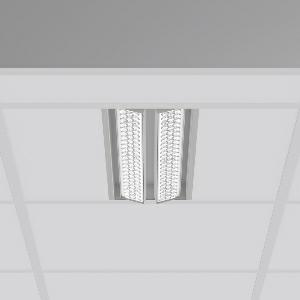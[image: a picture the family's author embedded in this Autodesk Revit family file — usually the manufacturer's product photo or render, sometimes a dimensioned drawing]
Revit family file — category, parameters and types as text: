
# Revit family: tx-move_901732_004_76_082e
name_source: partatom
category: Lighting Fixtures
units: mm (PartAtom-declared; Revit-internal decimal feet)

## family parameters
Cut with Voids When Loaded = No
Host = Face
Light Source = No
Part Type = Normal
Room Calculation Point = No
Round Connector Dimension = Use Diameter
Shared = No

## types (1)
- MultiLumen 1 (1 x LED Modul 830, 2750 lm, 3000)
    Apparent Load = 35 VA
    Approval mark = CE
    CIE Flux Codes = 90 97 99 100 100
    Color Rendering = 80
    Color Temperature = 3000
    Default Elevation = 1800 mm
    Description = Series: TX-MOVE
Einlege/Einbau-Flächenstrahler. Housing: sheet steel, powder-coated. 2xSwivel range: 90°. High-efficiency LED units with optimum light control thanks to clear plastic (PC) lens optics. Spezielle Mikrostrukturen reduzieren Gelbsaum. Symmetrical light distribution. Suitable for laying in grid ceiling module 600. Connected converter included in separate gearbox.Suitable for through-wiring.MultiLumen: Luminous flux adjustable in 3 steps. Accessories: Mounting frame for installation in suspended ceilings. Environmentally friendly and resource-saving due to replaceable and recyclable components. 
Colour: silver, matt (approx. RAL 9006)
Length: 597 mm
Width: 190 mm
Height: 39 mm
Cut-out length: 577.5 mm
Cut-out width: 174 mm
Recess height: 100 mm
Lamp: LED
Socket: without socket
Colour temperature: 3000K
Colour rendering index (CRI): 80
System power: 35 W
Rated luminous flux: 5500 lm
Luminous efficiency: 157 lm/W
System power 2: 47 W
Rated luminous flux 2: 7100 lm
Luminous efficiency 2: 151 lm/W
System power 3: 68 W
Rated luminous flux 3: 9700 lm
Luminous efficiency 3: 143 lm/W
Control gear: Dimmable EVG, DALI
Protection class: I
Type of protection: IP 20
    Height = 0 mm  [stored 0 ft]
    Lamp = 1 x LED Modul 830
    Lamp Light Flux = 2750 lm
    Lamp count = 1
    Length = 597 mm
    Lifetime = 50000 h
    Luminous efficacy = 157 lm/W
    Manufacturer = RZB
    ModVariant = No
    Model = 901732.004.76
    Mounting Place = Ceiling, Wall
    Mounting Type = Recessed
    Number of Poles = 1
    OnlyDefault = Yes
    Power Factor = 1
    Product Name = TX-MOVE
    Product group = Recessed projectors
    ProductGroupID = 401
    Protection Class = Protection class I
    Protection Degree = IP 20
    RLX_Detail_Level = 1
    RLX_Emergency_Light_Flux = 0 lm
    RLX_Emergency_Type = 0
    RLX_Emergency_Type_DB = No
    RlxData = <blob elided: 35609 chars, md5=0845f9e7>
    Socket = socket
    Standby Power = 0 W
    System Light Flux = 5500 lm
    System Power = 35 W
    Type Comments = MultiLumen 1
    Type Image = 901733.004.jpg
    URL = http://relux.com
    VarID = multilumen_1
    Voltage = 230 V
    Voltage Range = 220-240 V
    Weight = 0.00 kg
    Width = 190 mm  [stored 0.62336 ft]

note: [stored X ft] marks values corroborated as IEEE doubles in the binary element streams (Revit-internal decimal feet)

## geometry (parser evidence)
native form markers: Blend x4, Sweep x13
no freeform markers — native parametric forms only
